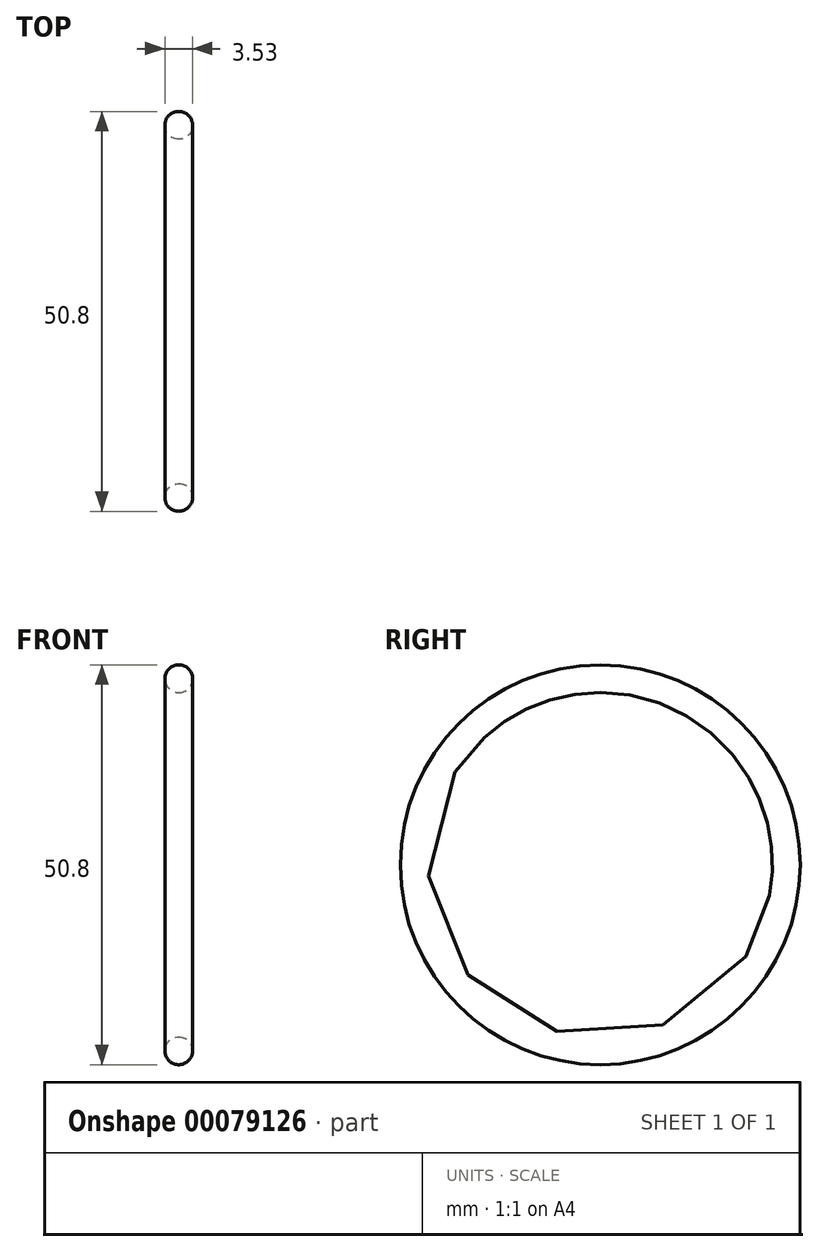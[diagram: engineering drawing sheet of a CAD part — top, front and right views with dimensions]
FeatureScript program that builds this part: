
annotation { "Feature Type Name" : "Feature", "Feature Type Description" : "" }
export const myFeature = defineFeature(function(context is Context, id is Id, definition is map)
    precondition{}
    {
        {
            var Q0;
            Q0=qCreatedBy(makeId("Front.planeOp"),FACE);
            var sketch = newSketch(context, id + "F0", { "sketchPlane" : qUnion([Q0])});
            skLineSegment(sketch, "E0", {"start": v(-22.26, 0) * mm, "end": v(33.4, 0) * mm});
            skCircle(sketch, "E1", {"center": v(10.59, 23.63) * mm, "radius": 1.77 * mm});
            skSolve(sketch);
        }
        {
            var Q0;
            Q0 = qSketchRegion(id + "F0", true);
            var Q1;
            Q1=sQuery(id+"F0.wireOp",EDGE,"E0");
            revolve(context, id + "F1", {"entities" : qUnion([Q0]), "axis" : qUnion([Q1]), "revolveType" : RevolveType.FULL});
        }
    });
